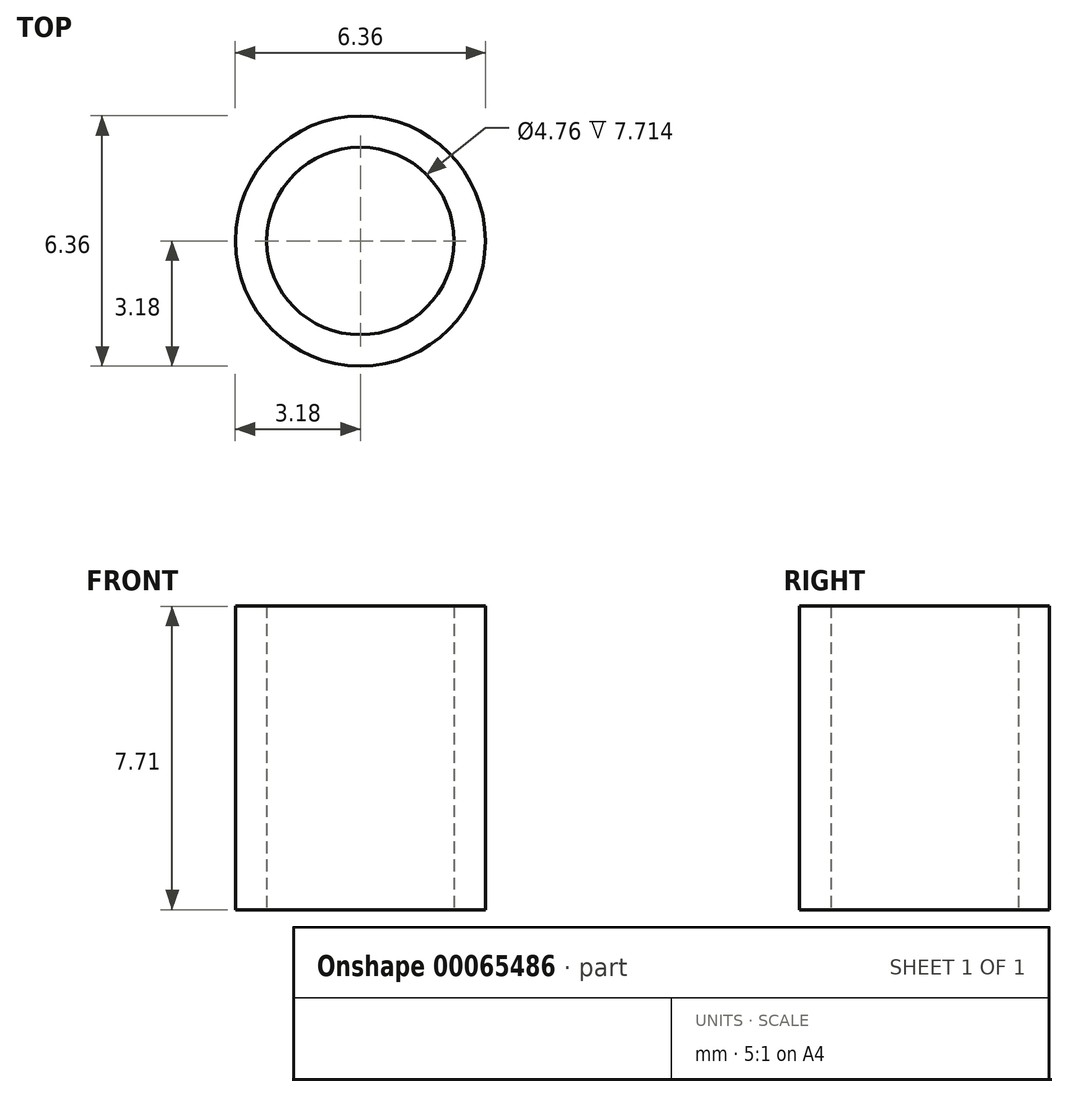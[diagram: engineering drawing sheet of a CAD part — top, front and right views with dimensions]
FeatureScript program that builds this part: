
annotation { "Feature Type Name" : "Feature", "Feature Type Description" : "" }
export const myFeature = defineFeature(function(context is Context, id is Id, definition is map)
    precondition{}
    {
        {
            var Q0;
            Q0=qCreatedBy(makeId("Top.planeOp"),FACE);
            var sketch = newSketch(context, id + "F0", { "sketchPlane" : qUnion([Q0])});
            skCircle(sketch, "E0", {"center": v(0, 0) * mm, "radius": 2.38 * mm});
            skCircle(sketch, "E1", {"center": v(0, 0) * mm, "radius": 3.18 * mm});
            skSolve(sketch);
        }
        {
            var Q0;
            Q0 = qSketchRegion(id + "F0", true);
            extrude(context, id + "F1", {"entities" : qUnion([Q0]), "depth" : 7.7 * mm});
        }
    });
